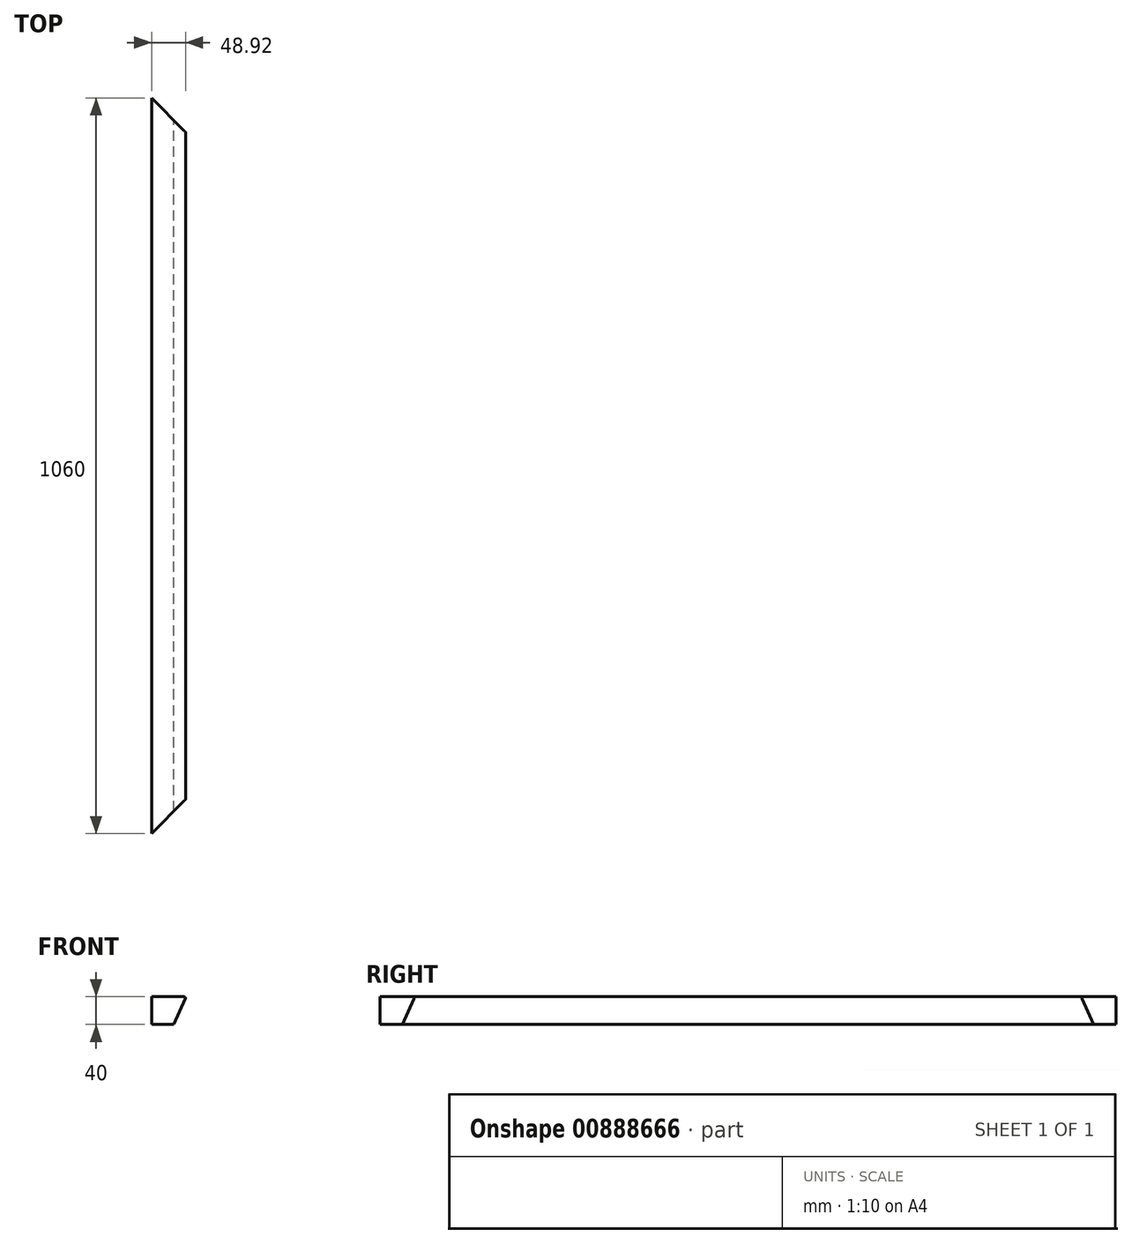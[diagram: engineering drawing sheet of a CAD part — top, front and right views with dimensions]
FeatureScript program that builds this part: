
annotation { "Feature Type Name" : "Feature", "Feature Type Description" : "" }
export const myFeature = defineFeature(function(context is Context, id is Id, definition is map)
    precondition{}
    {
        {
            var Q0;
            Q0=qCreatedBy(makeId("Front.planeOp"),FACE);
            var sketch = newSketch(context, id + "F0", { "sketchPlane" : qUnion([Q0])});
            skLineSegment(sketch, "E0.bottom", {"start": v(0, 0) * mm, "end": v(32.2, 0) * mm});
            skLineSegment(sketch, "E0.top", {"start": v(0, 40) * mm, "end": v(50, 40) * mm});
            skLineSegment(sketch, "E0.left", {"start": v(0, 0) * mm, "end": v(0, 40) * mm});
            skLineSegment(sketch, "E1", {"start": v(50, 40) * mm, "end": v(32.2, 0) * mm});
            skSolve(sketch);
        }
        {
            var Q0;
            Q0=qSketchRegion(id+"F0",true);
            extrude(context, id + "F1", {"entities" : qUnion([Q0]), "depth" : 1060 * mm, "offsetDistance" : 25 * mm});
        }
        {
            var Q0;
            Q0=makeQuery(id+"F1.opExtrude","SWEPT_EDGE",EDGE,{"disambiguationData":[OSD([sQuery(id+"F0.wireOp",EDGE,"E0.top"),sQuery(id+"F0.wireOp",EDGE,"E1")])]});
            fillet(context, id + "F2", {"entities" : qUnion([Q0]), "radius" : 2 * mm, "tangentPropagation" : true, "allowEdgeOverflow" : false});
        }
        {
            var Q0;
            Q0=makeQuery(id+"F1.opExtrude","SWEPT_FACE",FACE,{"disambiguationData":[OSD([sQuery(id+"F0.wireOp",EDGE,"E0.top")])]});
            var sketch = newSketch(context, id + "F3", { "sketchPlane" : qUnion([Q0])});
            skLineSegment(sketch, "E2", {"start": v(0, 0) * mm, "end": v(61.58, -61.58) * mm});
            skLineSegment(sketch, "E3", {"start": v(0, 0) * mm, "end": v(49.36, 0) * mm});
            skLineSegment(sketch, "E4", {"start": v(49.36, 0) * mm, "end": v(49.36, -49.36) * mm});
            skLineSegment(sketch, "E5", {"start": v(0, -1060) * mm, "end": v(60.14, -999.86) * mm});
            skLineSegment(sketch, "E6", {"start": v(0, -1060) * mm, "end": v(60.14, -1060) * mm});
            skLineSegment(sketch, "E7", {"start": v(60.14, -1060) * mm, "end": v(60.14, -999.86) * mm});
            skSolve(sketch);
        }
        {
            var Q0;
            Q0 = qSketchRegion(id + "F3", true);
            extrude(context, id + "F4", {"entities" : qUnion([Q0]), "operationType" : NewBodyOperationType.REMOVE, "endBound" : BoundingType.THROUGH_ALL, "oppositeDirection" : true, "depth" : 25 * mm, "offsetDistance" : 25 * mm});
        }
    });
